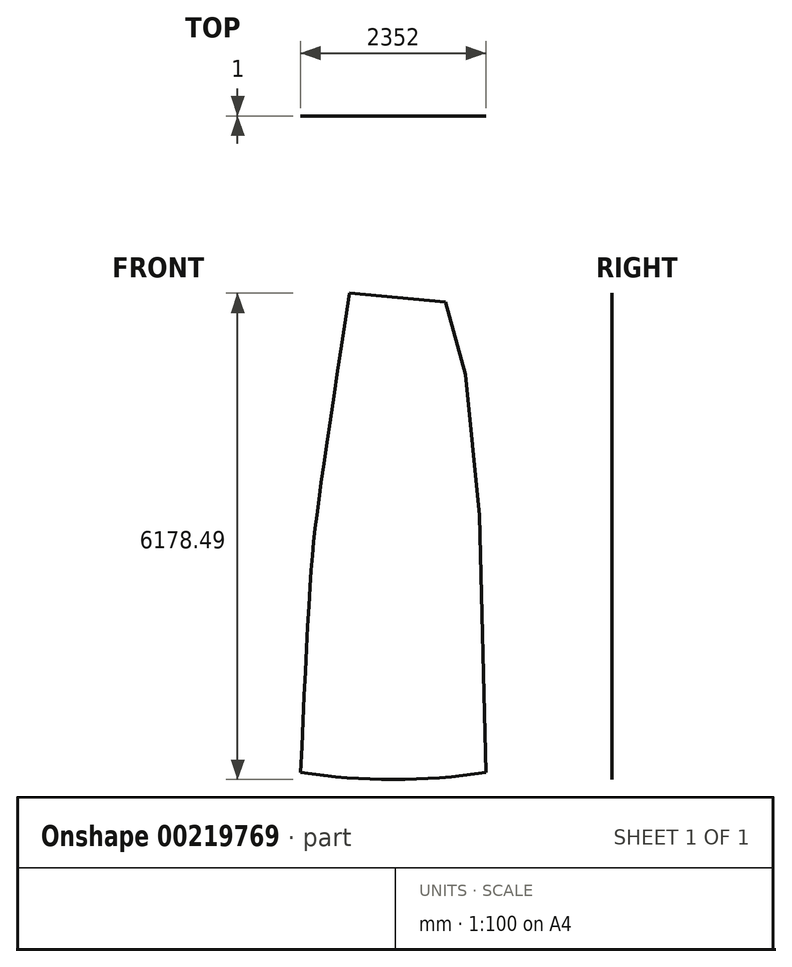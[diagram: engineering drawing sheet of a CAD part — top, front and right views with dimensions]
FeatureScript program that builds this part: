
annotation { "Feature Type Name" : "Feature", "Feature Type Description" : "" }
export const myFeature = defineFeature(function(context is Context, id is Id, definition is map)
    precondition{}
    {
        {
            var Q0;
            Q0=qCreatedBy(makeId("Front.planeOp"),FACE);
            var sketch = newSketch(context, id + "F0", { "sketchPlane" : qUnion([Q0])});
            skLineSegment(sketch, "E0", {"start": v(0, 0) * mm, "end": v(2352, 0) * mm});
            skLineSegment(sketch, "E1", {"start": v(0, 0) * mm, "end": v(620.2, 6088.5) * mm});
            skLineSegment(sketch, "E2", {"start": v(620.2, 6088.5) * mm, "end": v(2352, 0) * mm});
            skLineSegment(sketch, "E3", {"start": v(620.2, 6088.5) * mm, "end": v(1841.93, 6177.86) * mm});
            skLineSegment(sketch, "E4", {"start": v(1841.93, 6177.86) * mm, "end": v(2352, 0) * mm});
            skSolve(sketch);
        }
        {
            var Q0;
            Q0=makeQuery(id+"F0.imprint","IMPRINT",FACE,{"disambiguationData":[TD([[makeQuery(id+"F0.imprint","IMPRINT",EDGE,{"derivedFrom":sQuery(id+"F0.wireOp",EDGE,"E0")}),1.0]])]});
            var sketch = newSketch(context, id + "F1", { "sketchPlane" : qUnion([Q0])});
            skLineSegment(sketch, "E5", {"start": v(620.2, 6088.5) * mm, "end": v(1840.22, 5978.13) * mm});
            skLineSegment(sketch, "E6", {"start": v(1840.22, 5978.13) * mm, "end": v(2352, 0) * mm});
            skLineSegment(sketch, "E7", {"start": v(620.2, 6088.5) * mm, "end": v(2352, 0) * mm});
            skLineSegment(sketch, "E8", {"start": v(620.2, 6088.5) * mm, "end": v(0, 0) * mm});
            skSolve(sketch);
        }
        {
            var Q0;
            Q0=makeQuery(id+"F0.imprint","IMPRINT",FACE,{"disambiguationData":[TD([[makeQuery(id+"F0.imprint","IMPRINT",EDGE,{"derivedFrom":sQuery(id+"F0.wireOp",EDGE,"E0")}),1.0]])]});
            var sketch = newSketch(context, id + "F2", { "sketchPlane" : qUnion([Q0])});
            skArc(sketch, "E9", {"start": v(0, 0) * mm, "mid": v(1176, -90) * mm, "end": v(2352, 0) * mm});
            skLineSegment(sketch, "E10", {"start": v(620.2, 6088.5) * mm, "end": v(1840.22, 5978.13) * mm});
            skFitSpline(sketch, "E11", {"points": [v(0, 0) * mm, v(127.67, 2496.74) * mm, v(233.1, 3492.23) * mm, v(620.2, 6088.5) * mm], "startDerivative": vector(340.46, 7570.42) * mm, "endDerivative": vector(1177.6, 7705.28) * mm});
            skPoint(sketch, "E12", {"position": v(1486.1, 3044.25) * mm});
            skLineSegment(sketch, "E13", {"start": v(1486.1, 3044.25) * mm, "end": v(3056.8, 3491.02) * mm, "construction": true});
            skLineSegment(sketch, "E14", {"start": v(2271.45, 3267.63) * mm, "end": v(243.3, 3566.19) * mm, "construction": true});
            skLineSegment(sketch, "E15", {"start": v(620.2, 6088.5) * mm, "end": v(2271.45, 3267.63) * mm, "construction": true});
            skPoint(sketch, "E16", {"position": v(1445.82, 4678.06) * mm});
            skLineSegment(sketch, "E17", {"start": v(2091.02, 5055.74) * mm, "end": v(495.54, 5271.52) * mm, "construction": true});
            skLineSegment(sketch, "E18", {"start": v(1445.82, 4678.06) * mm, "end": v(2308.84, 5183.25) * mm, "construction": true});
            skLineSegment(sketch, "E19", {"start": v(2091.02, 5055.74) * mm, "end": v(620.2, 6088.5) * mm, "construction": true});
            skPoint(sketch, "E20", {"position": v(1355.6, 5572.12) * mm});
            skLineSegment(sketch, "E21", {"start": v(1355.6, 5572.12) * mm, "end": v(1930.26, 6390.52) * mm, "construction": true});
            skLineSegment(sketch, "E22", {"start": v(1652.3, 5994.67) * mm, "end": v(607.35, 6004.43) * mm, "construction": true});
            skLineSegment(sketch, "E23", {"start": v(2352, 0) * mm, "end": v(2271.45, 3267.63) * mm});
            skLineSegment(sketch, "E24", {"start": v(2091.02, 5055.74) * mm, "end": v(2271.45, 3267.63) * mm});
            skLineSegment(sketch, "E25", {"start": v(2091.02, 5055.74) * mm, "end": v(1840.22, 5978.13) * mm});
            skSolve(sketch);
        }
        {
            var Q0;
            Q0=qSketchRegion(id+"F2",true);
            extrude(context, id + "F3", {"entities" : qUnion([Q0]), "depth" : 1 * mm});
        }
    });
